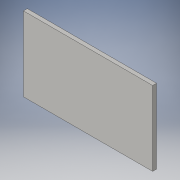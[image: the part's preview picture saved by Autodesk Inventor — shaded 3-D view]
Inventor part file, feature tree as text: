
AUTODESK INVENTOR PART (.ipt)
format: ipt  version: 2016 (Build 200138000, 138)  size: 88,064 bytes
history: native  units: in
note: dims shown in document units (in); Inventor stores cm internally (conversion verified against a paired STEP export)
features: extrude x1, sketch x1
ambient origin geometry x8: Origin, YZ Plane, XZ Plane, XY Plane, X Axis, Y Axis, Z Axis, Center Point
bodies: Solid1 (feature_tree)
feature tree (2):
  extrude  "Extrusion1"  Depth=0.5in TaperAngle=0.0deg
  sketch  "Sketch1"  dims[d0=16.5in d2=0.5in d3=0.0in]
